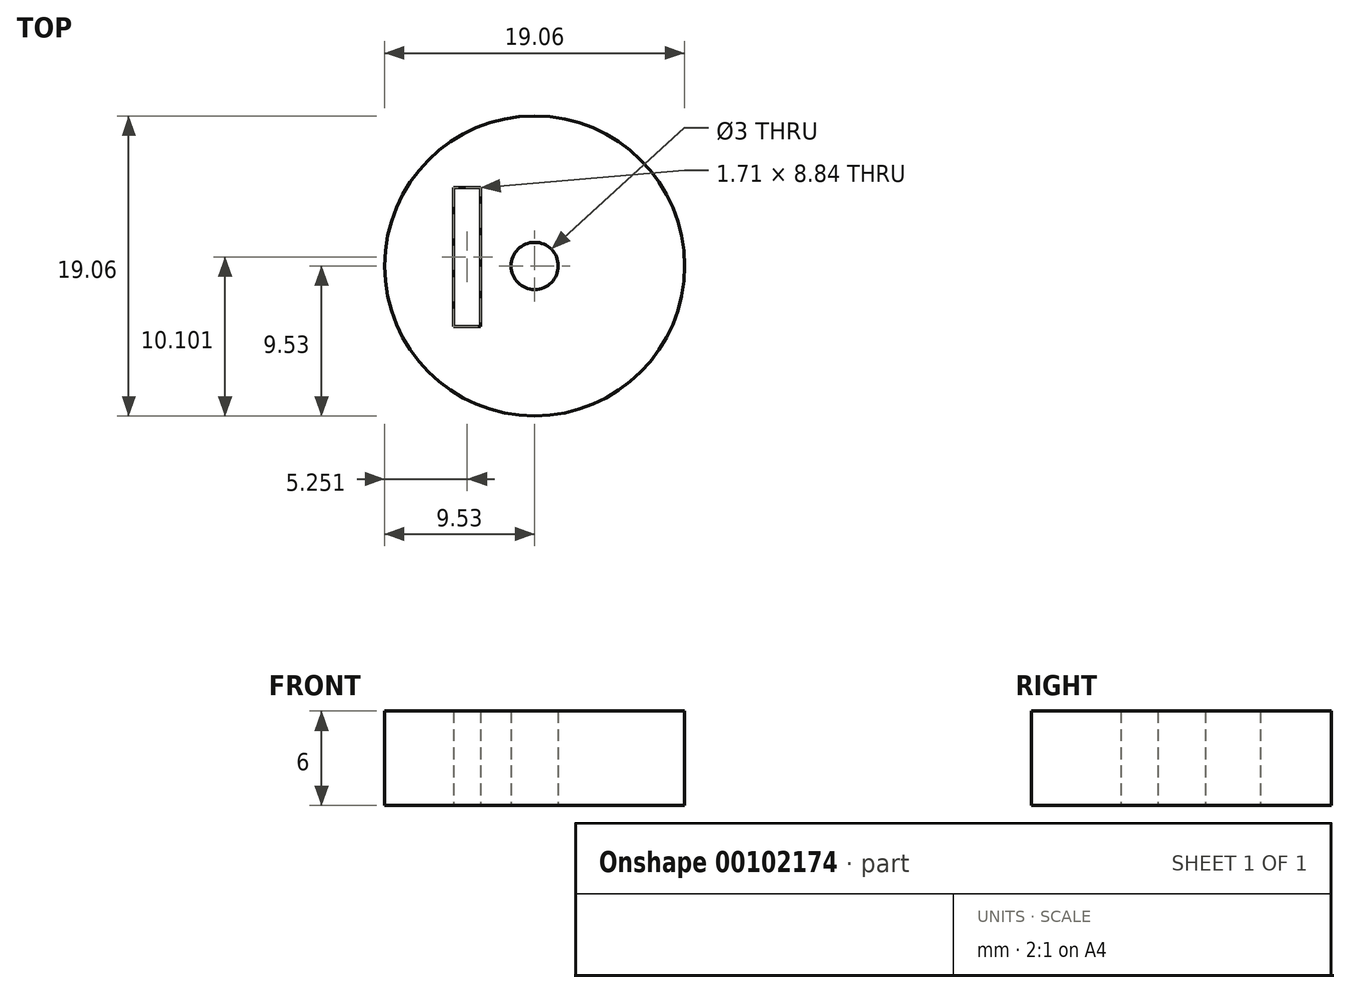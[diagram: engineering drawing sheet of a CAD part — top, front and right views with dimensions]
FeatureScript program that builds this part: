
annotation { "Feature Type Name" : "Feature", "Feature Type Description" : "" }
export const myFeature = defineFeature(function(context is Context, id is Id, definition is map)
    precondition{}
    {
        {
            var Q0;
            Q0=qCreatedBy(makeId("Top.planeOp"),FACE);
            var sketch = newSketch(context, id + "F0", { "sketchPlane" : qUnion([Q0])});
            skCircle(sketch, "E0", {"center": v(0, 0) * mm, "radius": 9.53 * mm});
            skCircle(sketch, "E1", {"center": v(0, 0) * mm, "radius": 1.5 * mm});
            skLineSegment(sketch, "E2.bottom", {"start": v(-3.42, 5) * mm, "end": v(-5.13, 5) * mm});
            skLineSegment(sketch, "E2.top", {"start": v(-3.42, -3.85) * mm, "end": v(-5.13, -3.85) * mm});
            skLineSegment(sketch, "E2.left", {"start": v(-3.42, 5) * mm, "end": v(-3.42, -3.85) * mm});
            skLineSegment(sketch, "E2.right", {"start": v(-5.13, 5) * mm, "end": v(-5.13, -3.85) * mm});
            skSolve(sketch);
        }
        {
            var Q0;
            Q0=makeQuery(id+"F0.imprint","IMPRINT",FACE,{"disambiguationData":[TD([[makeQuery(id+"F0.imprint","IMPRINT",EDGE,{"derivedFrom":sQuery(id+"F0.wireOp",EDGE,"E0")}),1.0]])]});
            extrude(context, id + "F1", {"entities" : qUnion([Q0]), "depth" : 6 * mm});
        }
    });
